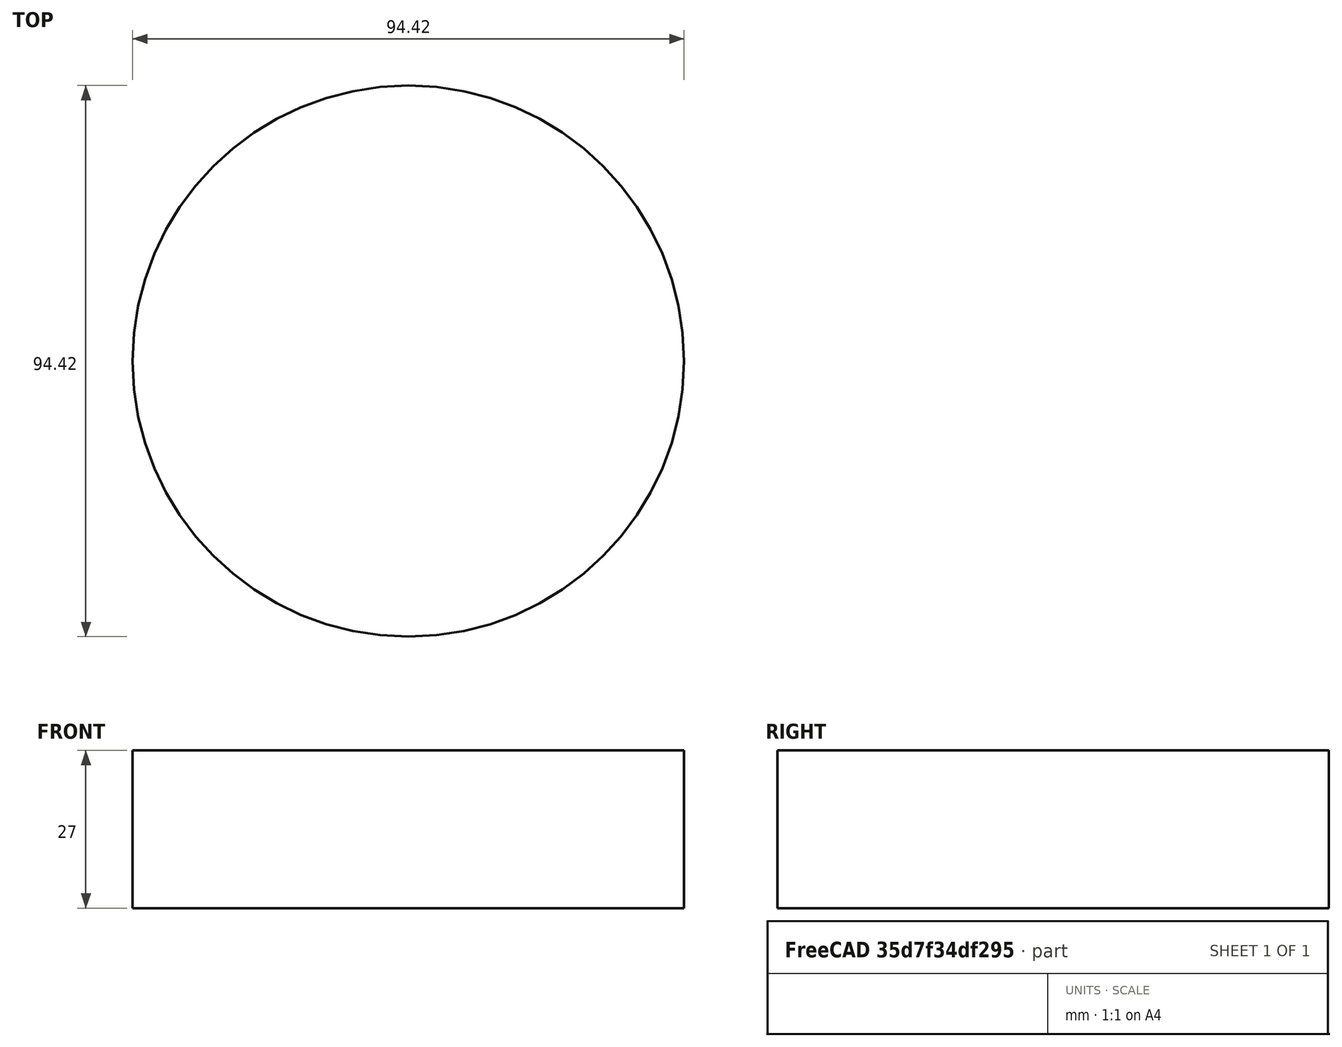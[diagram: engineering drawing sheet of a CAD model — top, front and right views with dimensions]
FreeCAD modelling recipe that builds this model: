
FCSTD DOCUMENT  (FreeCAD 0.20R29410 (Git))
Label: Cyl
License: All rights reserved
LicenseURL: http://en.wikipedia.org/wiki/All_rights_reserved
objects: App::DocumentObjectGroupPython×4, App::FeaturePython×2, Sketcher::SketchObject×1, PartDesign::Pad×1, PartDesign::Body×1
note: 4 computed .brp shape members not serialized (recipe doc carries the construction recipe); baked Part::Feature solids carry a one-line shape summary decoded from their .brp

FEATURE [Sketcher::SketchObject] Sketch
  FullyConstrained = false
  MapMode = 5
  Support = -> [XY_Plane]
  sketch-geometry (1):
    g0: Circle CenterX=0 CenterY=0 CenterZ=0 NormalX=0 NormalY=0 NormalZ=1 AngleXU=0 Radius=47.206
  constraints (1):
    c: Coincident(g0,g-1)
FEATURE [PartDesign::Pad] Pad
  Direction = (0,0,1)
  Length = 27
  Length2 = 10
  Profile = -> Sketch
  ReferenceAxis = -> Sketch [N_Axis]
  Type = 0
FEATURE [PartDesign::Body] Body
  Group = -> [Sketch,Pad]
  Origin = -> Origin
  Tip = -> Pad
FEATURE [App::DocumentObjectGroupPython] DS  # scripted group (container) (typed FeaturePython)
  Type = DS
FEATURE [App::FeaturePython] AnnotationPlane  label="AP1"  # WARN: FeaturePython — macro-defined, semantics opaque (R4)
  Direction = (0,0,1)
  PointWithOffset = (0,2.2e-15,27)
  Type = unkwon
  faces = -> Pad [Face3]
  p1 = (0,2.2e-15,27)
FEATURE [App::DocumentObjectGroupPython] Plane_AP1  # scripted group (container) (typed FeaturePython)
  Group = -> [AnnotationPlane]
  Type = Plane
FEATURE [App::DocumentObjectGroupPython] GDT  # scripted group (container) (typed FeaturePython)
  Group = -> [DS,Plane_AP1]
  Type = unkwon
FEATURE [App::FeaturePython] GeometricTolerance  label="GT1"  # WARN: FeaturePython — macro-defined, semantics opaque (R4)
  Characteristic = Perpendicularity
  CharacteristicCode = ⏊
  CharacteristicIcon = :/dd/icons/Characteristic/perpendicularity.svg
  Circumference = true
  FeatureControlFrame = Least material condition
  FeatureControlFrameCode = Ⓛ
  FeatureControlFrameIcon = :/dd/icons/FeatureControlFrame/leastMaterialCondition.svg
  ToleranceValue = 0.2
  Type = unkwon
FEATURE [App::DocumentObjectGroupPython] Annotation1  # scripted group (container) (typed FeaturePython)
  AP = -> AnnotationPlane
  Direction = (0,0,1)
  GT = -> [GeometricTolerance]
  Group = -> [GeometricTolerance]
  Type = unkwon
  circumferenceBool = false
  diameter = 94.4121
  faces = -> [Pad]
  highLimit = 0
  lowLimit = 0
  p1 = (0,2.2e-15,27)
  selectedPoint = (44,46,27)
  spBool = true
  toleranceDiameter = 0
  toleranceSelectBool = true
